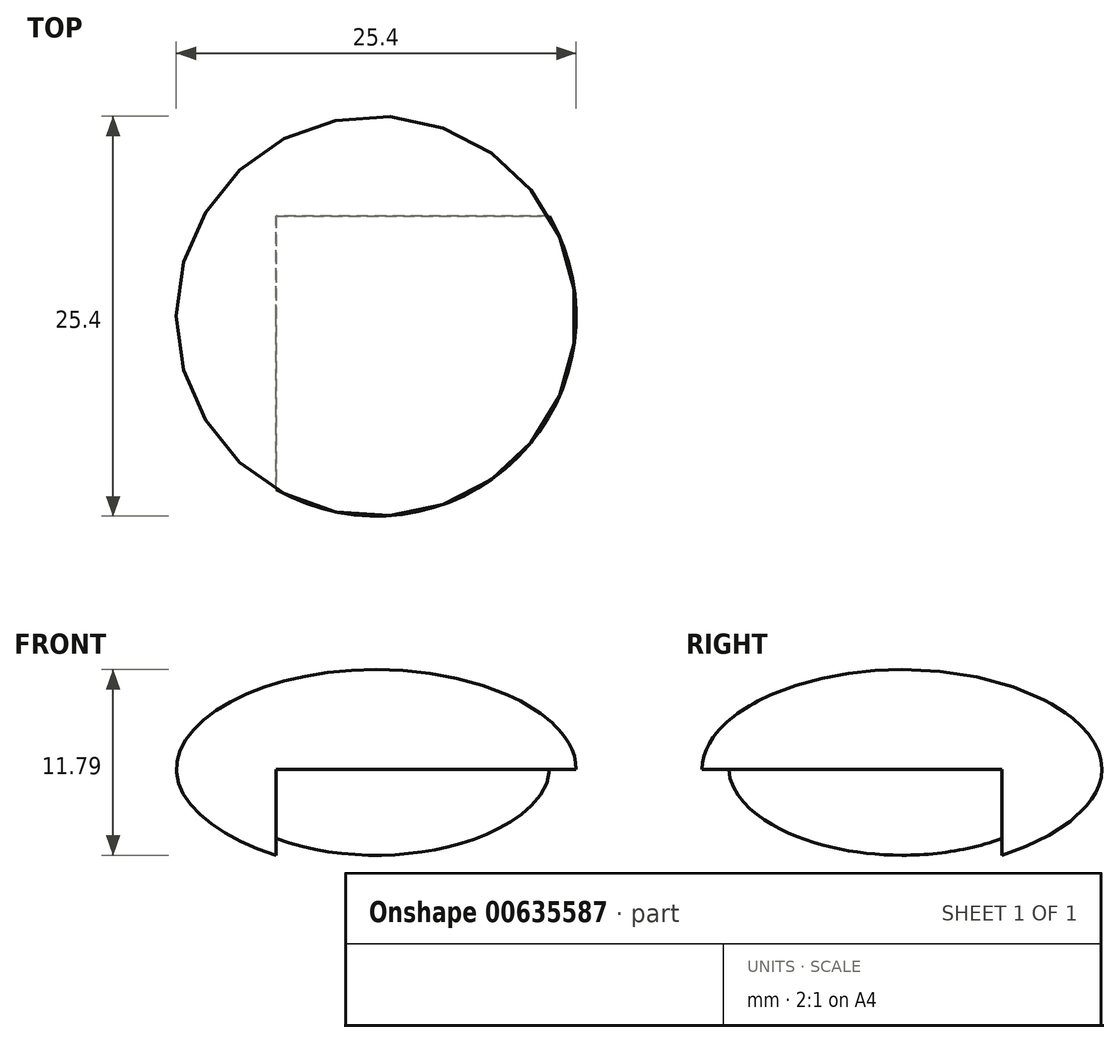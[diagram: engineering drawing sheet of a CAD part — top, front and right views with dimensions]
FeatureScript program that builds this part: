
annotation { "Feature Type Name" : "Feature", "Feature Type Description" : "" }
export const myFeature = defineFeature(function(context is Context, id is Id, definition is map)
    precondition{}
    {
        {
            var Q0;
            Q0=qCreatedBy(makeId("Front.planeOp"),FACE);
            var sketch = newSketch(context, id + "F0", { "sketchPlane" : qUnion([Q0])});
            skFitSpline(sketch, "E0", {"points": [v(0, 6.35) * mm, v(-12.7, 0) * mm, v(0, -6.35) * mm], "startDerivative": vector(-44.18, 0) * mm, "endDerivative": vector(42.72, 0) * mm});
            skLineSegment(sketch, "E1", {"start": v(0, 6.35) * mm, "end": v(0, -6.35) * mm});
            skSolve(sketch);
        }
        {
            var Q0;
            Q0=makeQuery(id+"F0.imprint","IMPRINT",FACE,{"disambiguationData":[TD([[makeQuery(id+"F0.imprint","IMPRINT",EDGE,{"derivedFrom":sQuery(id+"F0.wireOp",EDGE,"E0")}),1.0]])]});
            var Q1;
            Q1=sQuery(id+"F0.wireOp",EDGE,"E1");
            revolve(context, id + "F1", {"entities" : qUnion([Q0]), "axis" : qUnion([Q1]), "revolveType" : RevolveType.FULL});
        }
        {
            var Q0;
            Q0=qCreatedBy(makeId("Top.planeOp"),FACE);
            var sketch = newSketch(context, id + "F2", { "sketchPlane" : qUnion([Q0])});
            skLineSegment(sketch, "E2.bottom", {"start": v(-6.35, 6.35) * mm, "end": v(12.7, 6.35) * mm});
            skLineSegment(sketch, "E2.top", {"start": v(-6.35, -12.7) * mm, "end": v(12.7, -12.7) * mm});
            skLineSegment(sketch, "E2.left", {"start": v(-6.35, 6.35) * mm, "end": v(-6.35, -12.7) * mm});
            skLineSegment(sketch, "E2.right", {"start": v(12.7, 6.35) * mm, "end": v(12.7, -12.7) * mm});
            skSolve(sketch);
        }
        {
            var Q0;
            Q0=makeQuery(id+"F2.imprint","IMPRINT",FACE,{"disambiguationData":[TD([[makeQuery(id+"F2.imprint","IMPRINT",EDGE,{"derivedFrom":sQuery(id+"F2.wireOp",EDGE,"E2.bottom")}),-1.0]])]});
            extrude(context, id + "F3", {"entities" : qUnion([Q0]), "operationType" : NewBodyOperationType.REMOVE, "oppositeDirection" : true, "depth" : 6.35 * mm, "offsetDistance" : 25.4 * mm});
        }
    });
